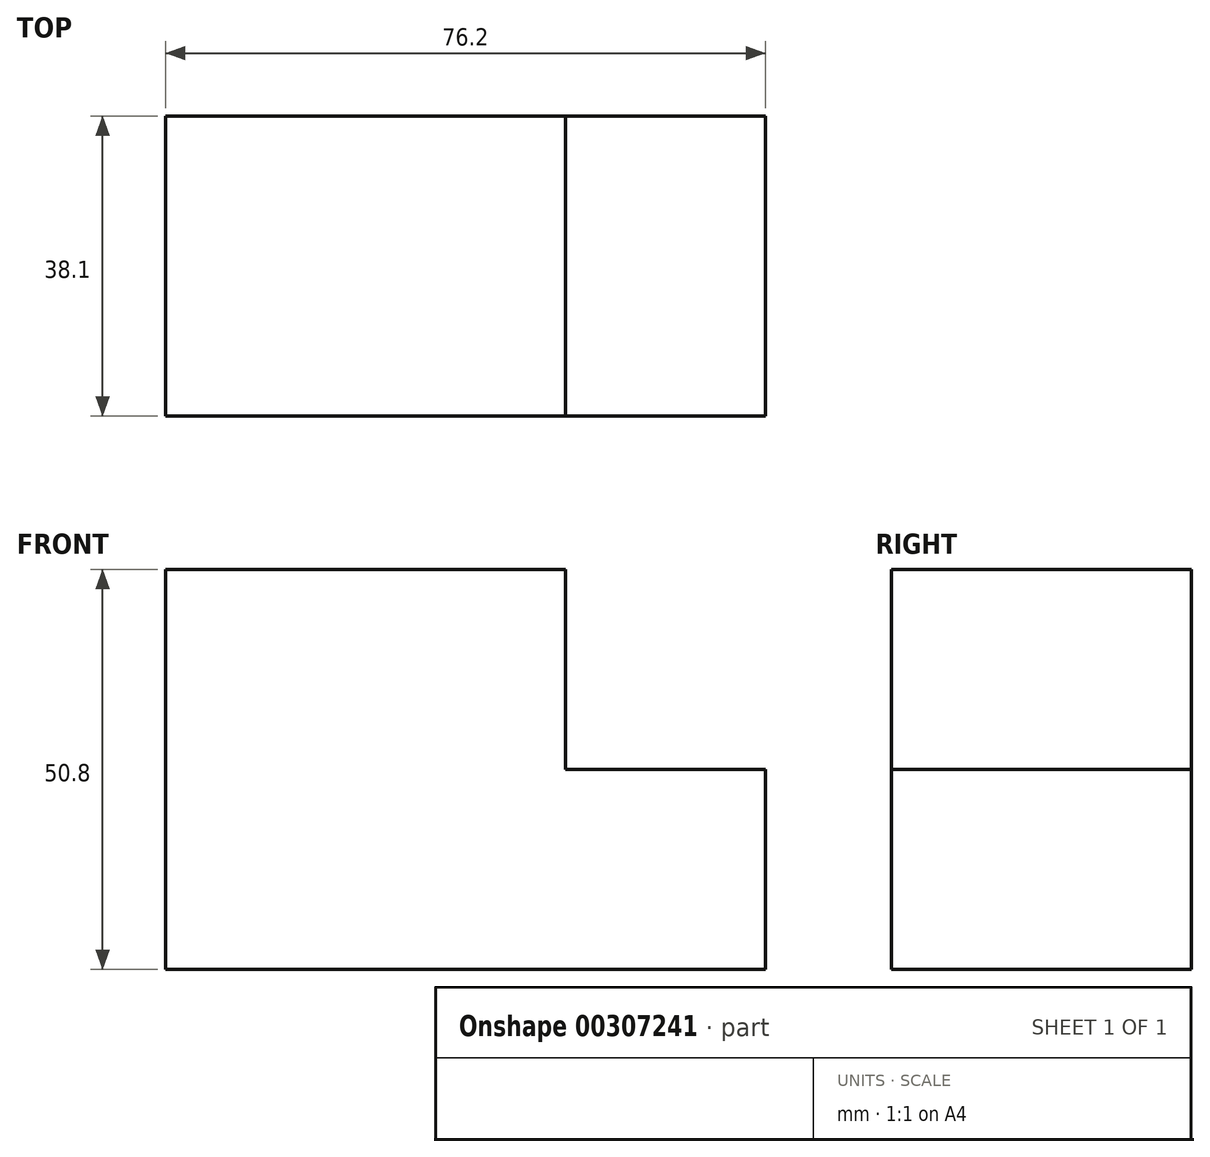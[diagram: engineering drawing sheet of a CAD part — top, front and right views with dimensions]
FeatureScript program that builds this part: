
annotation { "Feature Type Name" : "Feature", "Feature Type Description" : "" }
export const myFeature = defineFeature(function(context is Context, id is Id, definition is map)
    precondition{}
    {
        {
            var Q0;
            Q0=qCreatedBy(makeId("Front.planeOp"),FACE);
            var sketch = newSketch(context, id + "F0", { "sketchPlane" : qUnion([Q0])});
            skLineSegment(sketch, "E0", {"start": v(36.67, -41.7) * mm, "end": v(-39.53, -41.7) * mm});
            skLineSegment(sketch, "E1", {"start": v(36.67, -41.7) * mm, "end": v(36.67, -16.3) * mm});
            skLineSegment(sketch, "E2", {"start": v(36.67, -16.3) * mm, "end": v(11.27, -16.3) * mm});
            skLineSegment(sketch, "E3", {"start": v(11.27, -16.3) * mm, "end": v(11.27, 9.1) * mm});
            skLineSegment(sketch, "E4", {"start": v(-39.53, 9.1) * mm, "end": v(-39.53, -41.7) * mm});
            skLineSegment(sketch, "E5", {"start": v(-39.53, 9.1) * mm, "end": v(11.27, 9.1) * mm});
            skSolve(sketch);
        }
        {
            var Q0;
            Q0=makeQuery(id+"F0.imprint","IMPRINT",FACE,{"disambiguationData":[TD([[makeQuery(id+"F0.imprint","IMPRINT",EDGE,{"derivedFrom":sQuery(id+"F0.wireOp",EDGE,"E0")}),-1.0]])]});
            extrude(context, id + "F1", {"entities" : qUnion([Q0]), "depth" : 38.1 * mm});
        }
    });
